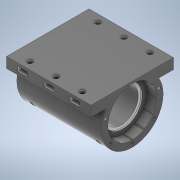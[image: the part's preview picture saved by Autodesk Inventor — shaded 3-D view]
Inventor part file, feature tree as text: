
AUTODESK INVENTOR PART (.ipt)
format: ipt  version: 2022 (Build 260153000, 153)  size: 551,424 bytes
history: native  units: mm
features: extrude x11, sketch x11, other x6, mirror x4, pattern_circular x2, fillet x1, projected_geometry x1
ambient origin geometry x8: Origin, YZ Plane, XZ Plane, XY Plane, X Axis, Y Axis, Z Axis, Center Point
bodies: Body1 (feature_tree)
feature tree (36):
  other  "Твердое тело1"
  extrude  "Выдавливание1"  Depth=26.0mm
  extrude  "Выдавливание2"  Depth=37.3mm
  extrude  "Выдавливание3"  Depth=50.0mm TaperAngle=0.0deg
  other  "РабПлоскость2"
  extrude  "Выдавливание4"  TaperAngle=0.0deg  [1 undecoded]
  other  "РабОсь1"
  pattern_circular  "Круговой массив1"  [2 undecoded]
  other  "РабПлоскость3"
  mirror  "Зеркальное отражение1"
  extrude  "Выдавливание5"  Depth=7.3mm TaperAngle=0.0deg
  extrude  "Выдавливание6"  Depth=2.2mm
  other  "РабПлоскость4"
  sketch  "Эскиз9"
  extrude  "Выдавливание9"  Depth=13.0mm TaperAngle=0.0deg
  fillet  "Сопряжение1"  [1 undecoded]
  pattern_circular  "Круговой массив2"  [2 undecoded]
  mirror  "Зеркальное отражение2"
  extrude  "Выдавливание10"  Depth=1.7mm TaperAngle=0.0deg
  mirror  "Зеркальное отражение3"
  other  "РабПлоскость5"
  extrude  "Выдавливание11"  Depth=50.0mm TaperAngle=210.0deg
  extrude  "Выдавливание12"  Depth=63.1mm
  mirror  "Зеркальное отражение4"
  extrude  "Выдавливание7"  Depth=8.0mm TaperAngle=0.0deg
  sketch  "Эскиз2"
  sketch  "Эскиз3"
  sketch  "Эскиз4"
  sketch  "Эскиз5"
  sketch  "Эскиз6"
  projected_geometry  "Спроецированная петля1"
  sketch  "Эскиз7"
  sketch  "Эскиз8"
  sketch  "Эскиз10"
  sketch  "Эскиз11"
  sketch  "Эскиз12"
note: 6 required parameter values undecoded (feature->parameter linkage not recoverable at this tier; creation-order binding heuristic only, values carry confidence <= 0.55)
